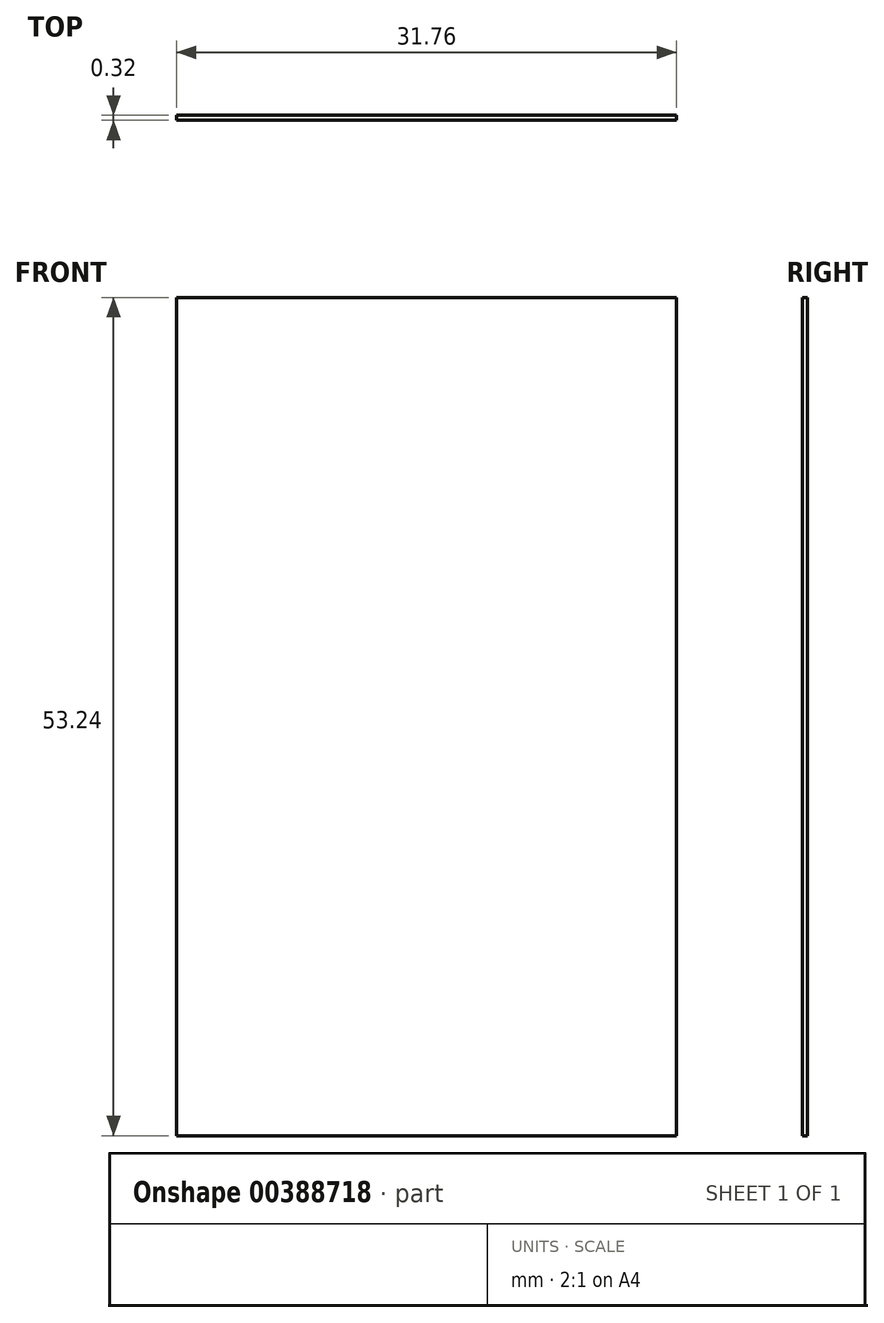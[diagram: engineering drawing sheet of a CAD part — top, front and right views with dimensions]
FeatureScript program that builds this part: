
annotation { "Feature Type Name" : "Feature", "Feature Type Description" : "" }
export const myFeature = defineFeature(function(context is Context, id is Id, definition is map)
    precondition{}
    {
        {
            var Q0;
            Q0=qCreatedBy(makeId("Front.planeOp"),FACE);
            var sketch = newSketch(context, id + "F0", { "sketchPlane" : qUnion([Q0])});
            skLineSegment(sketch, "E0.bottom", {"start": v(-15.88, -26.62) * mm, "end": v(15.88, -26.62) * mm});
            skLineSegment(sketch, "E0.top", {"start": v(-15.88, 26.62) * mm, "end": v(15.88, 26.62) * mm});
            skLineSegment(sketch, "E0.left", {"start": v(-15.88, -26.62) * mm, "end": v(-15.88, 26.62) * mm});
            skLineSegment(sketch, "E0.right", {"start": v(15.88, -26.62) * mm, "end": v(15.88, 26.62) * mm});
            skSolve(sketch);
        }
        {
            var Q0;
            Q0 = qSketchRegion(id + "F0", true);
            extrude(context, id + "F1", {"entities" : qUnion([Q0]), "depth" : 0.32 * mm});
        }
    });
